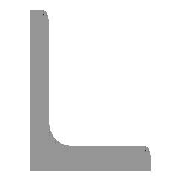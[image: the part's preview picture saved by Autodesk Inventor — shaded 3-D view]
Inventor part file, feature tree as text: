
AUTODESK INVENTOR PART (.ipt)
format: ipt  version: 2013 (Build 170138000, 138)  size: 129,536 bytes
history: native  units: mm (DEFAULTED — no unit token found)
features: other x4, plane x3, split x2, sketch x2
ambient origin geometry x8: Origin, YZ Plane, XZ Plane, XY Plane, X Axis, Y Axis, Z Axis, Center Point
bodies: Solid1 (feature_tree), Body (feature_tree)
feature tree (11):
  parser-record x1  (decoder bookkeeping rows leaked as tree rows — omitted from the tree; the rows remain in map.json)
  other  "Driven Length"
  other  "Start plane"
  other  "End plane"
  plane  "Work Plane4"
  split  "Split1"
  plane  "Work Plane5"
  split  "Split2"
  sketch  "Sketch3"  dims[d0=38.1mm]
  plane  "Work Plane3"
  sketch  "Sketch4"  dims[d1=38.1mm d2=4.7625mm d3=4.7625mm d4=1092.2mm d5=0.0mm d10=0.0mm d11=0.0mm d12=-0.0mm d13=1092.2mm d14=4.826mm d15=2.286mm d16=90.0deg d17=1092.2mm]
